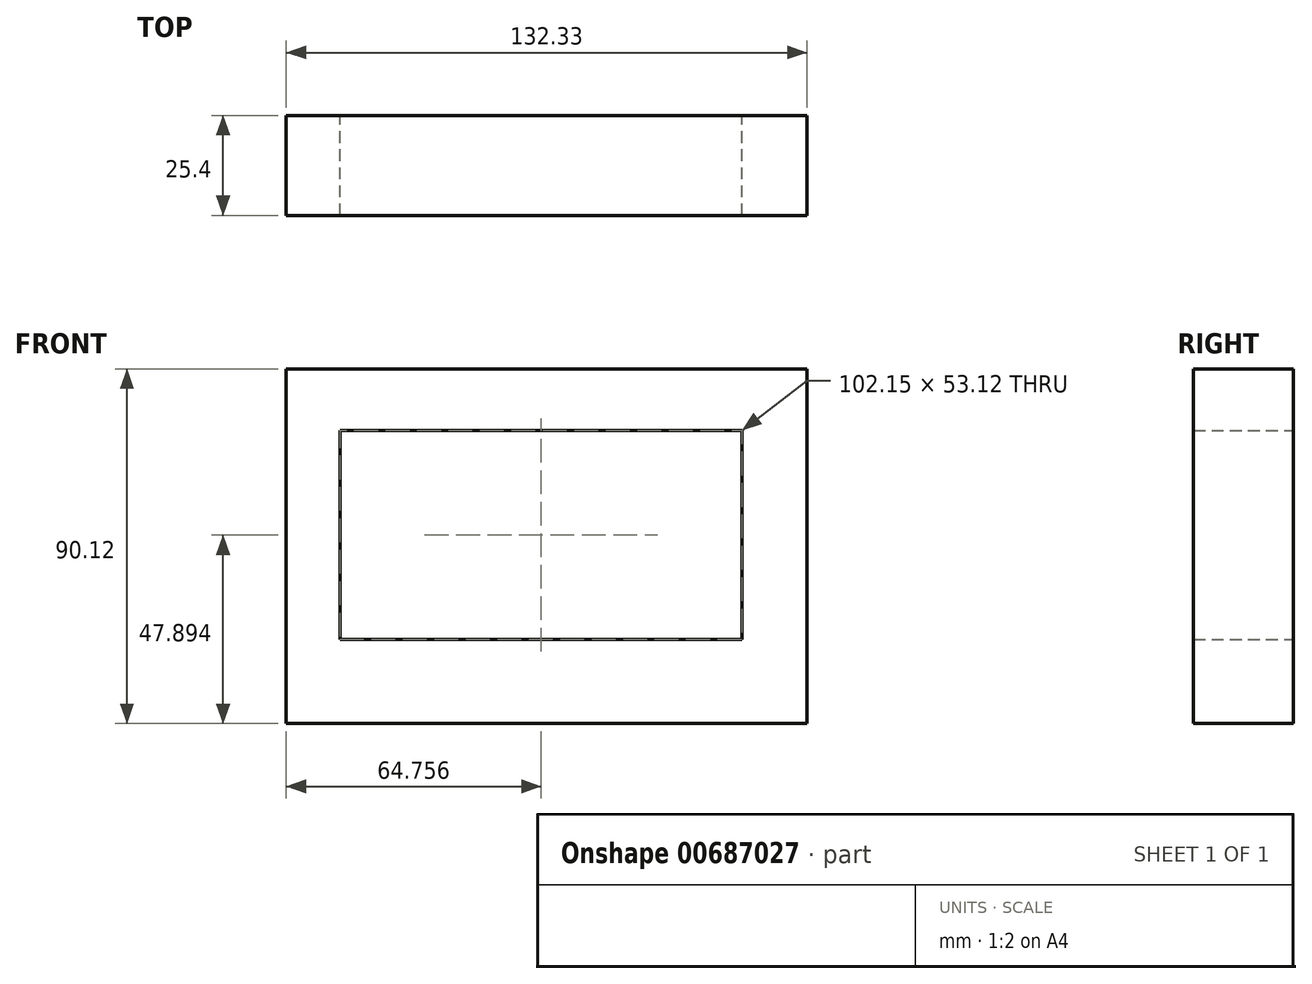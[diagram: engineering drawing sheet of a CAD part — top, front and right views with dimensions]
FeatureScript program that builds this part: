
annotation { "Feature Type Name" : "Feature", "Feature Type Description" : "" }
export const myFeature = defineFeature(function(context is Context, id is Id, definition is map)
    precondition{}
    {
        {
            var Q0;
            Q0=qCreatedBy(makeId("Front.planeOp"),FACE);
            var sketch = newSketch(context, id + "F0", { "sketchPlane" : qUnion([Q0])});
            skLineSegment(sketch, "E0.bottom", {"start": v(-46.99, 15.32) * mm, "end": v(55.16, 15.32) * mm});
            skLineSegment(sketch, "E0.top", {"start": v(-46.99, -37.8) * mm, "end": v(55.16, -37.8) * mm});
            skLineSegment(sketch, "E0.left", {"start": v(-46.99, 15.32) * mm, "end": v(-46.99, -37.8) * mm});
            skLineSegment(sketch, "E0.right", {"start": v(55.16, 15.32) * mm, "end": v(55.16, -37.8) * mm});
            skLineSegment(sketch, "E1.bottom", {"start": v(-60.67, 31) * mm, "end": v(71.66, 31) * mm});
            skLineSegment(sketch, "E1.top", {"start": v(-60.67, -59.13) * mm, "end": v(71.66, -59.13) * mm});
            skLineSegment(sketch, "E1.left", {"start": v(-60.67, 31) * mm, "end": v(-60.67, -59.13) * mm});
            skLineSegment(sketch, "E1.right", {"start": v(71.66, 31) * mm, "end": v(71.66, -59.13) * mm});
            skSolve(sketch);
        }
        {
            var Q0;
            Q0=makeQuery(id+"F0.imprint","IMPRINT",FACE,{"disambiguationData":[TD([[makeQuery(id+"F0.imprint","IMPRINT",EDGE,{"derivedFrom":sQuery(id+"F0.wireOp",EDGE,"E0.bottom")}),1.0]])]});
            extrude(context, id + "F1", {"entities" : qUnion([Q0]), "depth" : 25.4 * mm, "offsetDistance" : 25.4 * mm});
        }
    });
